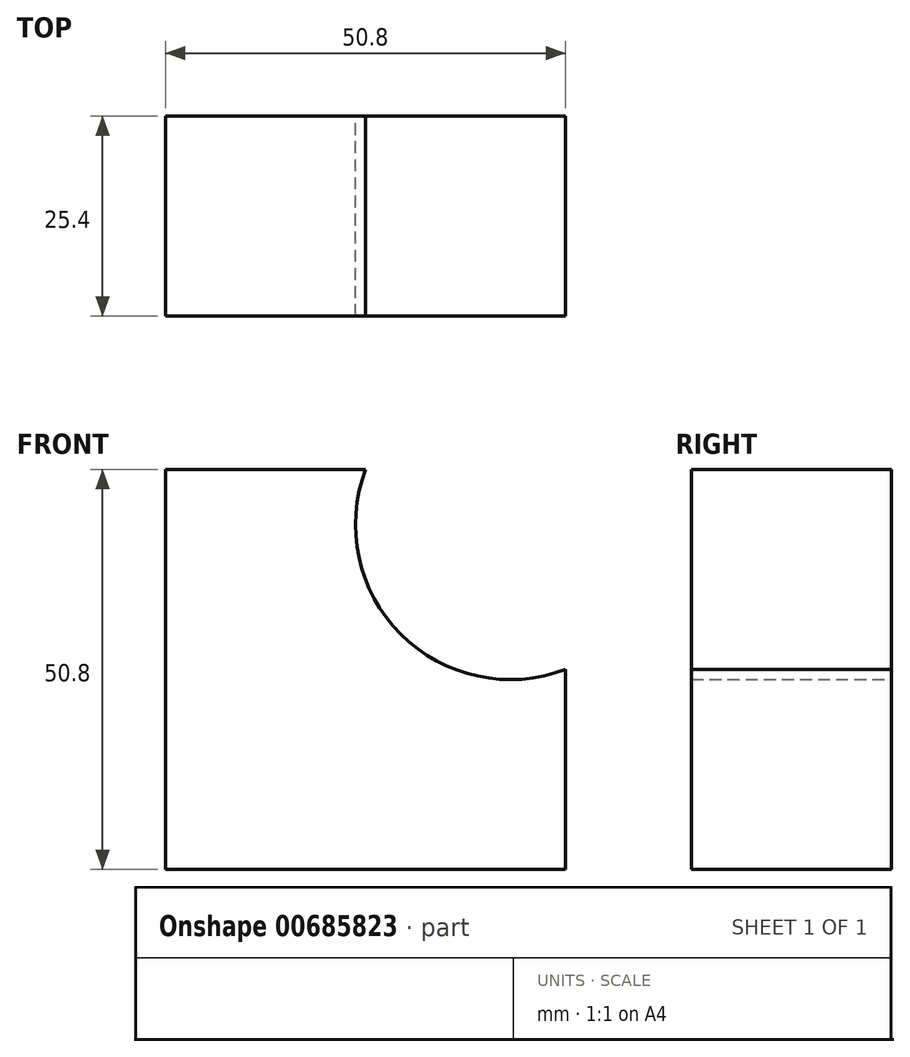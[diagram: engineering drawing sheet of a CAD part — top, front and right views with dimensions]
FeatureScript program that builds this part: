
annotation { "Feature Type Name" : "Feature", "Feature Type Description" : "" }
export const myFeature = defineFeature(function(context is Context, id is Id, definition is map)
    precondition{}
    {
        {
            var Q0;
            Q0=qCreatedBy(makeId("Front.planeOp"),FACE);
            var sketch = newSketch(context, id + "F0", { "sketchPlane" : qUnion([Q0])});
            skLineSegment(sketch, "E0", {"start": v(-57, 39.06) * mm, "end": v(-57, -11.74) * mm});
            skLineSegment(sketch, "E1", {"start": v(-57, -11.74) * mm, "end": v(-6.2, -11.74) * mm});
            skLineSegment(sketch, "E2", {"start": v(-6.2, -11.74) * mm, "end": v(-6.2, 13.66) * mm});
            skLineSegment(sketch, "E3", {"start": v(-57, 39.06) * mm, "end": v(-31.6, 39.06) * mm});
            skArc(sketch, "E4", {"start": v(-31.6, 39.06) * mm, "mid": v(-27.12, 18.14) * mm, "end": v(-6.2, 13.66) * mm});
            skSolve(sketch);
        }
        {
            var Q0;
            Q0=makeQuery(id+"F0.imprint","IMPRINT",FACE,{"disambiguationData":[TD([[makeQuery(id+"F0.imprint","IMPRINT",EDGE,{"derivedFrom":sQuery(id+"F0.wireOp",EDGE,"E0")}),1.0]])]});
            extrude(context, id + "F1", {"entities" : qUnion([Q0]), "depth" : 25.4 * mm, "offsetDistance" : 25.4 * mm});
        }
    });
